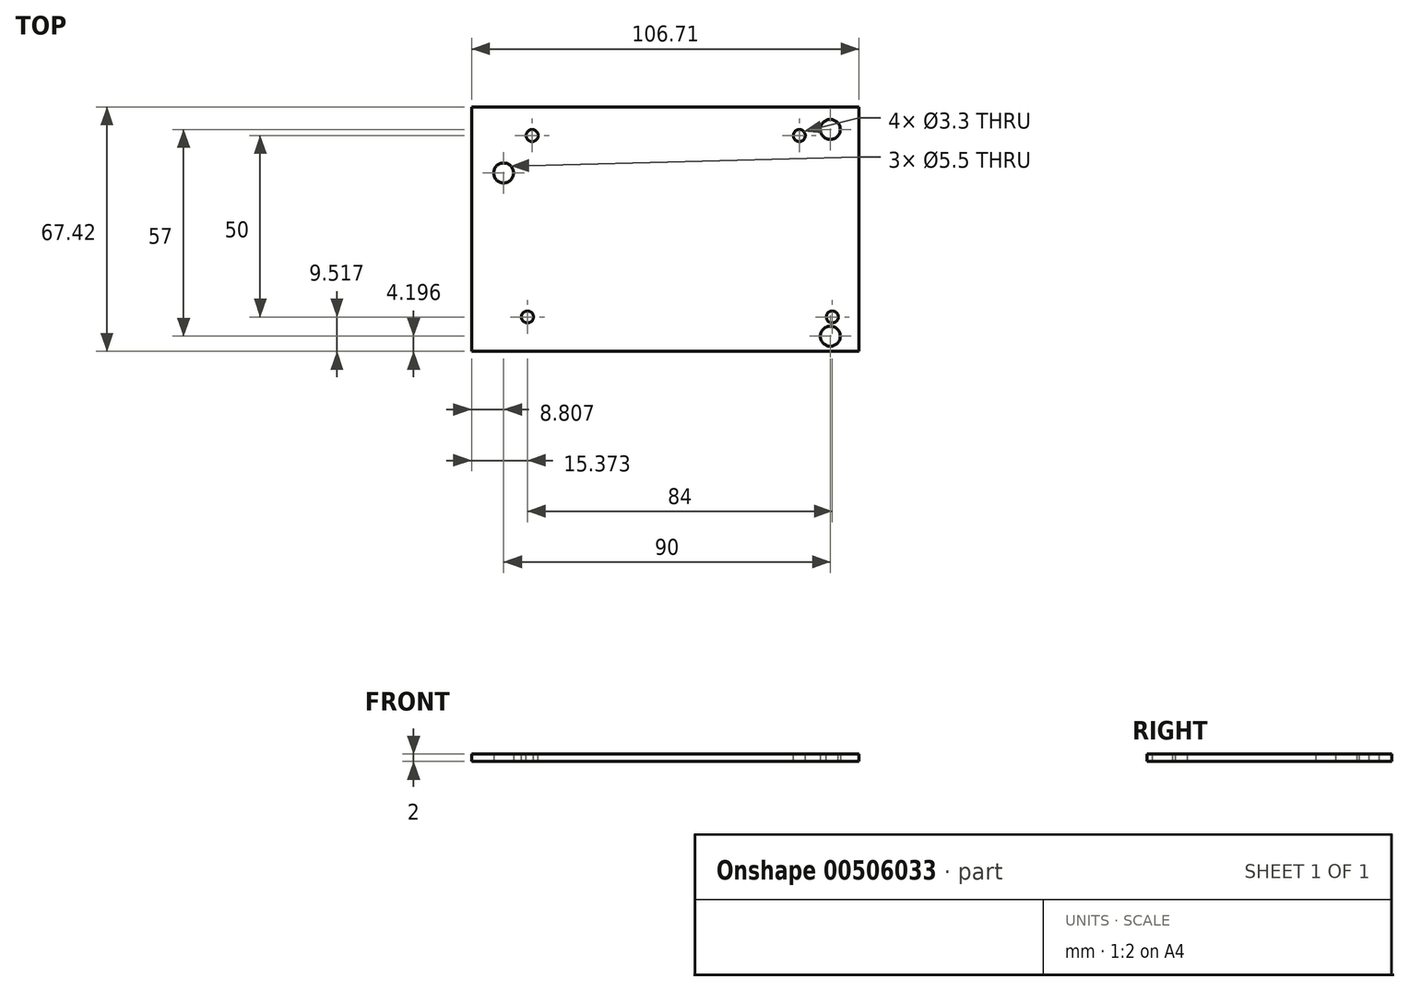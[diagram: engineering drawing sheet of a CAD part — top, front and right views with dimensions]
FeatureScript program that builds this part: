
annotation { "Feature Type Name" : "Feature", "Feature Type Description" : "" }
export const myFeature = defineFeature(function(context is Context, id is Id, definition is map)
    precondition{}
    {
        {
            var Q0;
            Q0=qCreatedBy(makeId("Top.planeOp"),FACE);
            var sketch = newSketch(context, id + "F0", { "sketchPlane" : qUnion([Q0])});
            skLineSegment(sketch, "E0.bottom", {"start": v(-64.3, 29) * mm, "end": v(25.7, 29) * mm, "construction": true});
            skLineSegment(sketch, "E0.top", {"start": v(-64.3, -28) * mm, "end": v(25.7, -28) * mm, "construction": true});
            skLineSegment(sketch, "E0.left", {"start": v(-64.3, 29) * mm, "end": v(-64.3, -28) * mm, "construction": true});
            skLineSegment(sketch, "E0.right", {"start": v(25.7, 29) * mm, "end": v(25.7, -28) * mm, "construction": true});
            skLineSegment(sketch, "E1", {"start": v(-64.3, 17) * mm, "end": v(37.1, 17) * mm, "construction": true});
            skLineSegment(sketch, "E2.bottom", {"start": v(-73.11, 35.22) * mm, "end": v(33.6, 35.22) * mm});
            skLineSegment(sketch, "E2.top", {"start": v(-73.11, -32.2) * mm, "end": v(33.6, -32.2) * mm});
            skLineSegment(sketch, "E2.left", {"start": v(-73.11, 35.22) * mm, "end": v(-73.11, -32.2) * mm});
            skLineSegment(sketch, "E2.right", {"start": v(33.6, 35.22) * mm, "end": v(33.6, -32.2) * mm});
            skSolve(sketch);
        }
        {
            var Q0;
            Q0 = qSketchRegion(id + "F0", true);
            extrude(context, id + "F1", {"entities" : qUnion([Q0]), "depth" : 2 * mm});
        }
        {
            var Q0;
            Q0=sQuery(id+"F0.wireOp",VERTEX,"E1.start");
            var Q1;
            Q1=sQuery(id+"F0.wireOp",VERTEX,"E0.right.start");
            var Q2;
            Q2=sQuery(id+"F0.wireOp",VERTEX,"E0.right.end");
            var Q3;
            Q3=makeQuery(id+"F1.opExtrude","SWEPT_BODY",BODY,{"disambiguationData":[OSD([sQuery(id+"F0.wireOp",EDGE,"E2.bottom"),sQuery(id+"F0.wireOp",EDGE,"E2.top"),sQuery(id+"F0.wireOp",EDGE,"E2.left"),sQuery(id+"F0.wireOp",EDGE,"E2.right")])]});
            hole(context, id + "F2", {"style" : HoleStyle.SIMPLE, "endStyle" : HoleEndStyle.BLIND, "oppositeDirection" : true, "standardTappedOrClearance" : lookupTablePath({ "standard" : "ISO", "fit" : "Normal", "size" : "M5", "type" : "Clearance" }), "standardBlindInLast" : lookupTablePath({ "fit" : "Standard", "standard" : "ISO", "size" : "M5", "type" : "Clearance" }), "holeDiameter" : 5.5 * mm, "holeDepth" : 18 * mm, "isTappedThrough" : true, "tappedDepth" : 12 * mm, "tapClearance" : 3, "startFromSketch" : true, "locations" : qUnion([Q0, Q1, Q2]), "scope" : qUnion([Q3])});
        }
        {
            var Q0;
            Q0=makeQuery(id+"F1.opExtrude","CAP_FACE",FACE,{"disambiguationData":[OSD([sQuery(id+"F0.wireOp",EDGE,"E2.bottom"),sQuery(id+"F0.wireOp",EDGE,"E2.top"),sQuery(id+"F0.wireOp",EDGE,"E2.left"),sQuery(id+"F0.wireOp",EDGE,"E2.right")])],"isStart":false});
            var sketch = newSketch(context, id + "F3", { "sketchPlane" : qUnion([Q0])});
            skLineSegment(sketch, "E3.bottom", {"start": v(-57.74, 27.32) * mm, "end": v(17.16, 27.32) * mm, "construction": true});
            skLineSegment(sketch, "E3.top", {"start": v(-57.74, -22.68) * mm, "end": v(17.16, -22.68) * mm, "construction": true});
            skLineSegment(sketch, "E3.left", {"start": v(-57.74, 27.32) * mm, "end": v(-57.74, -22.68) * mm, "construction": true});
            skLineSegment(sketch, "E3.right", {"start": v(17.16, 27.32) * mm, "end": v(17.16, -22.68) * mm, "construction": true});
            skLineSegment(sketch, "E4.0", {"start": v(-56.44, 27.32) * mm, "end": v(-56.44, -22.68) * mm, "construction": true});
            skPoint(sketch, "E5", {"position": v(26.26, -22.68) * mm});
            skSolve(sketch);
        }
        {
            var Q0;
            Q0=sQuery(id+"F3.wireOp",VERTEX,"E4.0.start");
            var Q1;
            Q1=sQuery(id+"F3.wireOp",VERTEX,"E3.bottom.end");
            var Q2;
            Q2=sQuery(id+"F3.wireOp",VERTEX,"E3.top.start");
            var Q3;
            Q3=sQuery(id+"F3.wireOp",VERTEX,"E5");
            var Q4;
            Q4=makeQuery(id+"F1.opExtrude","SWEPT_BODY",BODY,{"disambiguationData":[OSD([sQuery(id+"F0.wireOp",EDGE,"E2.bottom"),sQuery(id+"F0.wireOp",EDGE,"E2.top"),sQuery(id+"F0.wireOp",EDGE,"E2.left"),sQuery(id+"F0.wireOp",EDGE,"E2.right")])]});
            hole(context, id + "F4", {"style" : HoleStyle.SIMPLE, "endStyle" : HoleEndStyle.BLIND, "standardTappedOrClearance" : lookupTablePath({ "standard" : "ISO", "fit" : "Normal", "size" : "M3", "type" : "Clearance" }), "standardBlindInLast" : lookupTablePath({ "fit" : "Standard", "standard" : "ISO", "size" : "M3", "type" : "Clearance" }), "holeDiameter" : 3.3 * mm, "holeDepth" : 18 * mm, "isTappedThrough" : true, "tappedDepth" : 12 * mm, "tapClearance" : 3, "startFromSketch" : true, "locations" : qUnion([Q0, Q1, Q2, Q3]), "scope" : qUnion([Q4])});
        }
    });
